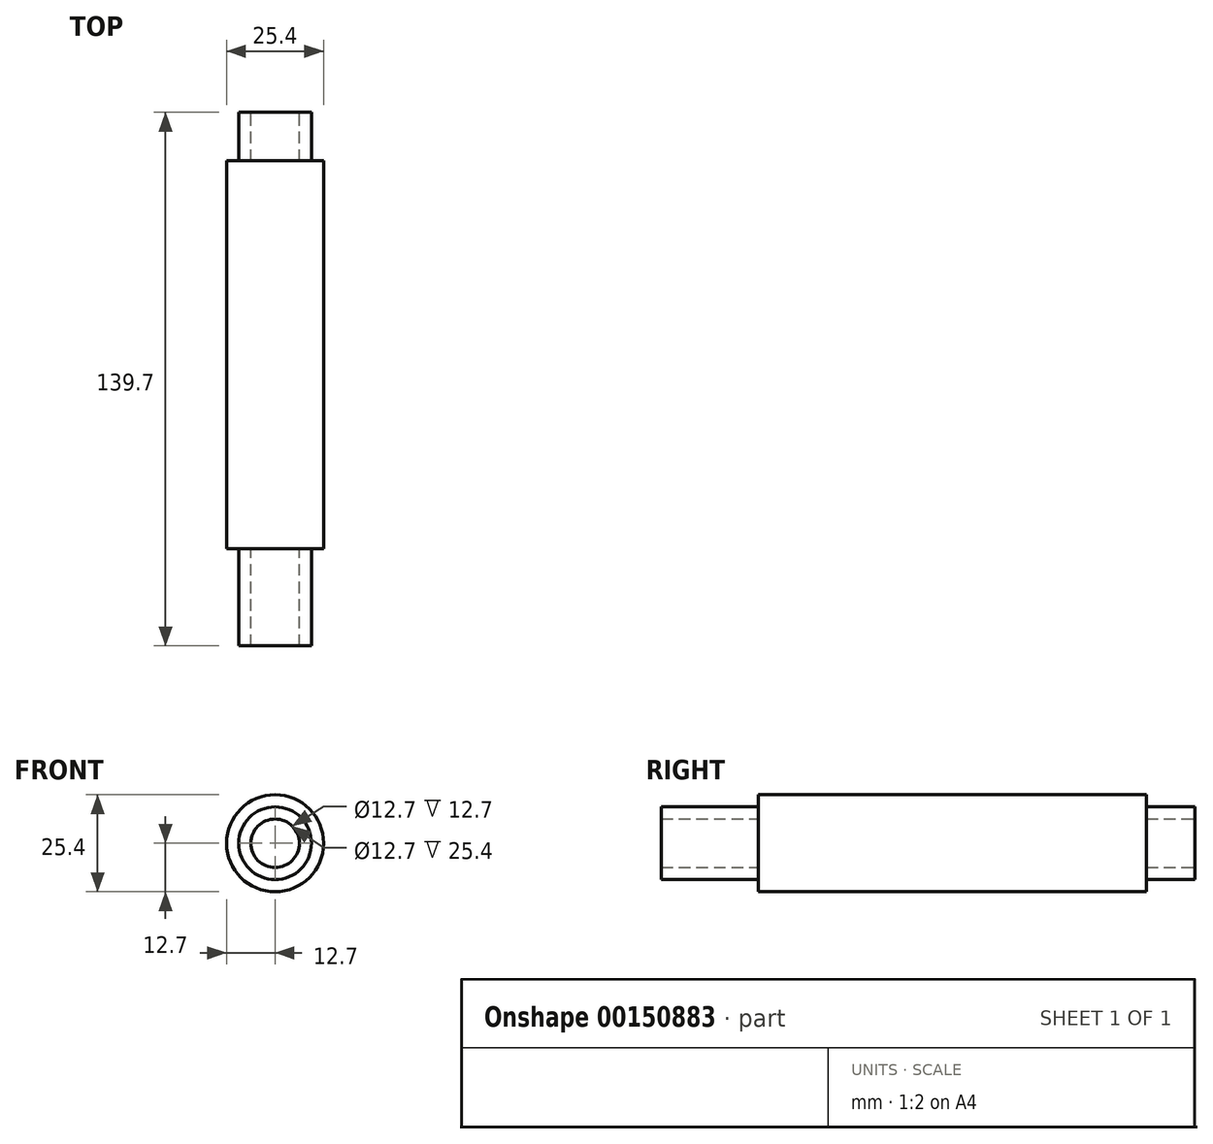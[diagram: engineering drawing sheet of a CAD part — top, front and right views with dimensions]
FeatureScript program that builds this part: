
annotation { "Feature Type Name" : "Feature", "Feature Type Description" : "" }
export const myFeature = defineFeature(function(context is Context, id is Id, definition is map)
    precondition{}
    {
        {
            var Q0;
            Q0=qCreatedBy(makeId("Front.planeOp"),FACE);
            var sketch = newSketch(context, id + "F0", { "sketchPlane" : qUnion([Q0])});
            skCircle(sketch, "E0", {"center": v(0, 0) * mm, "radius": 9.53 * mm});
            skCircle(sketch, "E1", {"center": v(0, 0) * mm, "radius": 6.35 * mm});
            skSolve(sketch);
        }
        {
            var Q0;
            Q0 = qSketchRegion(id + "F0", true);
            extrude(context, id + "F1", {"entities" : qUnion([Q0]), "depth" : 12.7 * mm});
        }
        {
            var Q0;
            Q0=makeQuery(id+"F1.opExtrude","CAP_FACE",FACE,{"disambiguationData":[OSD([sQuery(id+"F0.wireOp",EDGE,"E0"),sQuery(id+"F0.wireOp",EDGE,"E1")])],"isStart":false});
            var sketch = newSketch(context, id + "F2", { "sketchPlane" : qUnion([Q0])});
            skCircle(sketch, "E2", {"center": v(0, 0) * mm, "radius": 12.7 * mm});
            skSolve(sketch);
        }
        {
            var Q0;
            Q0 = qSketchRegion(id + "F2", true);
            extrude(context, id + "F3", {"entities" : qUnion([Q0]), "operationType" : NewBodyOperationType.ADD, "depth" : 101.6 * mm});
        }
        {
            var Q0;
            Q0=makeQuery(id+"F3.opExtrude","CAP_FACE",FACE,{"disambiguationData":[OSD([sQuery(id+"F2.wireOp",EDGE,"E2")])],"isStart":false});
            var sketch = newSketch(context, id + "F4", { "sketchPlane" : qUnion([Q0])});
            skCircle(sketch, "E3", {"center": v(0, 0) * mm, "radius": 9.53 * mm});
            skCircle(sketch, "E4", {"center": v(0, 0) * mm, "radius": 6.35 * mm});
            skSolve(sketch);
        }
        {
            var Q0;
            Q0 = qSketchRegion(id + "F4", true);
            extrude(context, id + "F5", {"entities" : qUnion([Q0]), "operationType" : NewBodyOperationType.ADD, "depth" : 25.4 * mm});
        }
    });
